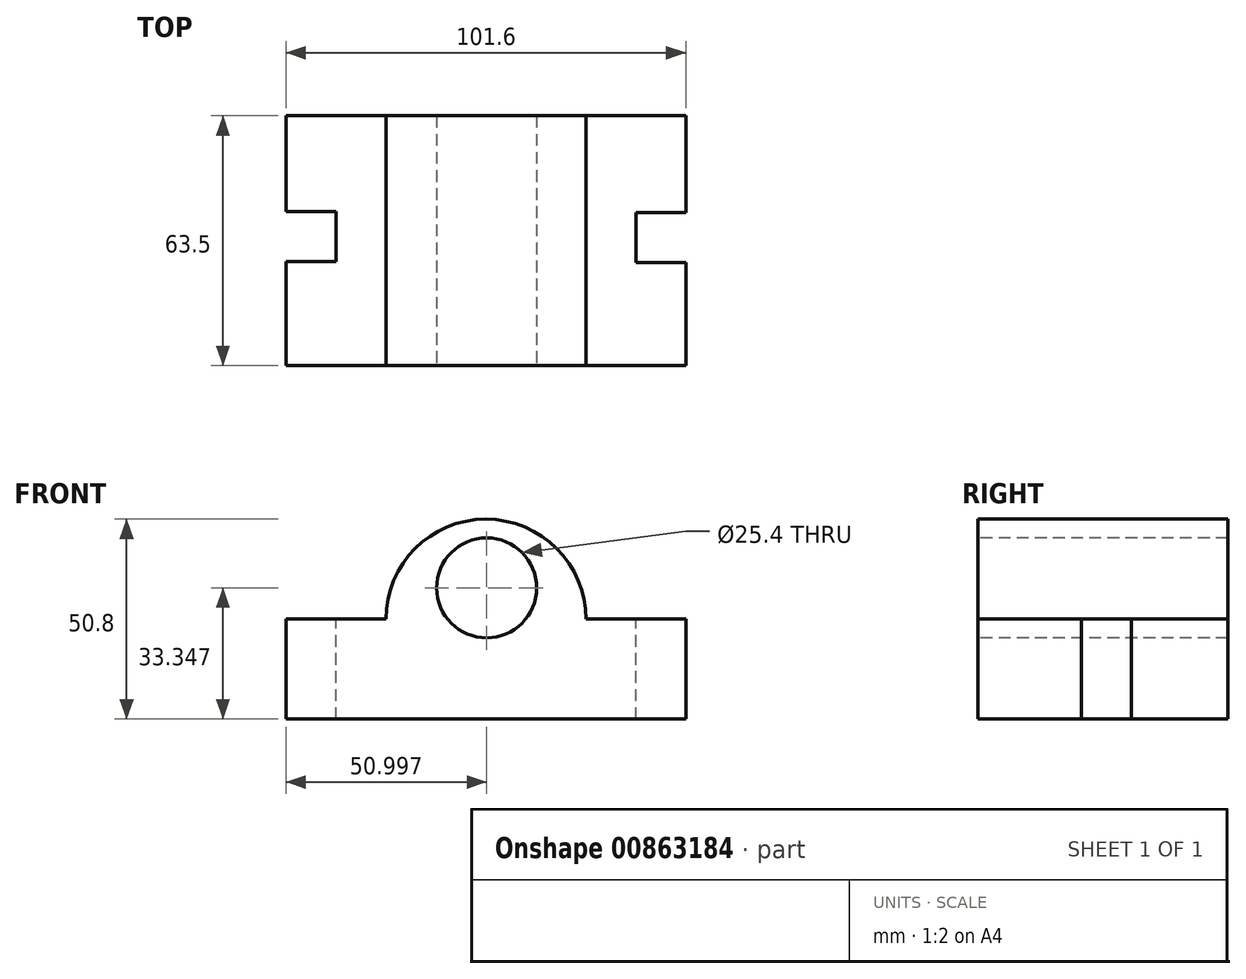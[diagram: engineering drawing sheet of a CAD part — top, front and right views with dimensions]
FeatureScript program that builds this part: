
annotation { "Feature Type Name" : "Feature", "Feature Type Description" : "" }
export const myFeature = defineFeature(function(context is Context, id is Id, definition is map)
    precondition{}
    {
        {
            var Q0;
            Q0=qCreatedBy(makeId("Front.planeOp"),FACE);
            var sketch = newSketch(context, id + "F0", { "sketchPlane" : qUnion([Q0])});
            skLineSegment(sketch, "E0", {"start": v(0, 0) * mm, "end": v(101.6, 0) * mm});
            skLineSegment(sketch, "E1", {"start": v(101.6, 0) * mm, "end": v(101.6, 25.4) * mm});
            skLineSegment(sketch, "E2", {"start": v(0, 0) * mm, "end": v(0, 25.4) * mm});
            skLineSegment(sketch, "E3", {"start": v(0, 25.4) * mm, "end": v(25.4, 25.4) * mm});
            skLineSegment(sketch, "E4", {"start": v(101.6, 25.4) * mm, "end": v(76.2, 25.4) * mm});
            skArc(sketch, "E5", {"start": v(76.2, 25.4) * mm, "mid": v(50.8, 50.8) * mm, "end": v(25.4, 25.4) * mm});
            skSolve(sketch);
        }
        {
            var Q0;
            Q0 = qSketchRegion(id + "F0", true);
            extrude(context, id + "F1", {"entities" : qUnion([Q0]), "depth" : 63.5 * mm, "offsetDistance" : 25.4 * mm});
        }
        {
            var Q0;
            Q0=makeQuery(id+"F1.opExtrude","SWEPT_FACE",FACE,{"disambiguationData":[OSD([sQuery(id+"F0.wireOp",EDGE,"E3")])]});
            var sketch = newSketch(context, id + "F2", { "sketchPlane" : qUnion([Q0])});
            skLineSegment(sketch, "E6", {"start": v(0, -24.38) * mm, "end": v(12.7, -24.38) * mm});
            skLineSegment(sketch, "E7", {"start": v(12.7, -24.38) * mm, "end": v(12.7, -37.08) * mm});
            skLineSegment(sketch, "E8", {"start": v(12.7, -37.08) * mm, "end": v(0, -37.08) * mm});
            skLineSegment(sketch, "E9", {"start": v(100.6, -25.11) * mm, "end": v(87.9, -25.11) * mm});
            skLineSegment(sketch, "E10", {"start": v(87.9, -25.11) * mm, "end": v(87.9, -37.81) * mm});
            skLineSegment(sketch, "E11", {"start": v(87.9, -37.81) * mm, "end": v(100.6, -37.81) * mm});
            skSolve(sketch);
        }
        {
            var Q0;
            {var subQ0=sQuery(id+"F2.wireOp",EDGE,"E6");Q0=makeQuery(id+"F2.imprint","IMPRINT",FACE,{"disambiguationData":[TD([[makeQuery(id+"F2.imprint","IMPRINT",EDGE,{"derivedFrom":subQ0}),-1.0]])]});}
            extrude(context, id + "F3", {"entities" : qUnion([Q0]), "operationType" : NewBodyOperationType.REMOVE, "endBound" : BoundingType.THROUGH_ALL, "oppositeDirection" : true, "depth" : 25.4 * mm, "offsetDistance" : 25.4 * mm});
        }
        {
            var Q0;
            Q0=makeQuery(id+"F1.opExtrude","SWEPT_FACE",FACE,{"disambiguationData":[OSD([sQuery(id+"F0.wireOp",EDGE,"E4")])]});
            var sketch = newSketch(context, id + "F4", { "sketchPlane" : qUnion([Q0])});
            skLineSegment(sketch, "E12", {"start": v(101.6, -24.53) * mm, "end": v(88.9, -24.53) * mm});
            skLineSegment(sketch, "E13", {"start": v(88.9, -24.53) * mm, "end": v(88.9, -37.23) * mm});
            skLineSegment(sketch, "E14", {"start": v(88.9, -37.23) * mm, "end": v(101.6, -37.23) * mm});
            skSolve(sketch);
        }
        {
            var Q0;
            Q0 = qSketchRegion(id + "F4", true);
            var Q1;
            {var subQ0=sQuery(id+"F4.wireOp",EDGE,"E12");Q1=makeQuery(id+"F4.imprint","IMPRINT",FACE,{"disambiguationData":[TD([[makeQuery(id+"F4.imprint","IMPRINT",EDGE,{"derivedFrom":subQ0}),1.0]])]});}
            extrude(context, id + "F5", {"entities" : qUnion([Q0, Q1]), "operationType" : NewBodyOperationType.REMOVE, "endBound" : BoundingType.THROUGH_ALL, "oppositeDirection" : true, "depth" : 25.4 * mm, "offsetDistance" : 25.4 * mm});
        }
        {
            var Q0;
            Q0=makeQuery(id+"F1.opExtrude","CAP_FACE",FACE,{"disambiguationData":[OSD([sQuery(id+"F0.wireOp",EDGE,"E0"),sQuery(id+"F0.wireOp",EDGE,"E1"),sQuery(id+"F0.wireOp",EDGE,"E2"),sQuery(id+"F0.wireOp",EDGE,"E3"),sQuery(id+"F0.wireOp",EDGE,"E4"),sQuery(id+"F0.wireOp",EDGE,"E5")])],"isStart":false});
            var sketch = newSketch(context, id + "F6", { "sketchPlane" : qUnion([Q0])});
            skCircle(sketch, "E15", {"center": v(51, 33.35) * mm, "radius": 12.7 * mm});
            skSolve(sketch);
        }
        {
            var Q0;
            Q0=makeQuery(id+"F6.imprint","IMPRINT",FACE,{"disambiguationData":[TD([[makeQuery(id+"F6.imprint","IMPRINT",EDGE,{"derivedFrom":sQuery(id+"F6.wireOp",EDGE,"E15")}),1.0]])]});
            extrude(context, id + "F7", {"entities" : qUnion([Q0]), "operationType" : NewBodyOperationType.REMOVE, "endBound" : BoundingType.THROUGH_ALL, "oppositeDirection" : true, "depth" : 25.4 * mm, "offsetDistance" : 25.4 * mm});
        }
    });
